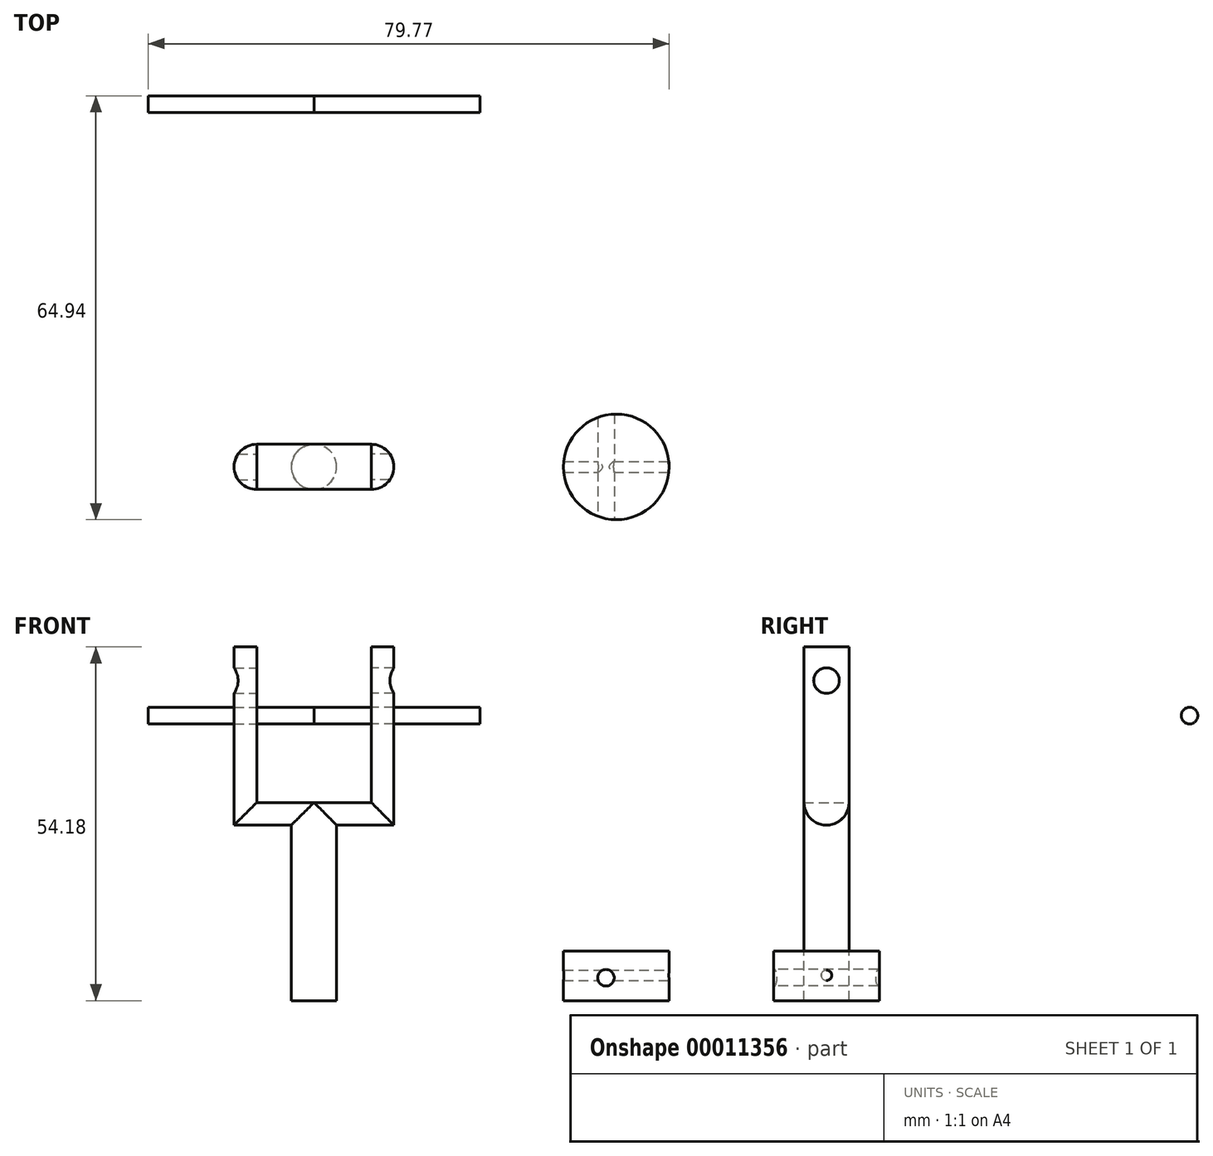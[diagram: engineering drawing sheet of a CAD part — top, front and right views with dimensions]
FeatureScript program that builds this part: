
annotation { "Feature Type Name" : "Feature", "Feature Type Description" : "" }
export const myFeature = defineFeature(function(context is Context, id is Id, definition is map)
    precondition{}
    {
        {
            var Q0;
            Q0=qCreatedBy(makeId("Front.planeOp"),FACE);
            var sketch = newSketch(context, id + "F0", { "sketchPlane" : qUnion([Q0])});
            skLineSegment(sketch, "E0", {"start": v(0, 0) * mm, "end": v(0, 30.36) * mm});
            skLineSegment(sketch, "E1", {"start": v(0, 30.36) * mm, "end": v(8.77, 30.36) * mm});
            skLineSegment(sketch, "E2", {"start": v(8.77, 30.36) * mm, "end": v(8.77, 54.18) * mm});
            skSolve(sketch);
        }
        {
            var Q0;
            Q0=qCreatedBy(makeId("Top.planeOp"),FACE);
            var sketch = newSketch(context, id + "F1", { "sketchPlane" : qUnion([Q0])});
            skArc(sketch, "E3", {"start": v(0, -3.46) * mm, "mid": v(3.46, 0) * mm, "end": v(0, 3.46) * mm});
            skLineSegment(sketch, "E4", {"start": v(0, 3.46) * mm, "end": v(0, -3.46) * mm});
            skSolve(sketch);
        }
        {
            var Q0;
            Q0=makeQuery(id+"F1.imprint","IMPRINT",FACE,{"disambiguationData":[TD([[makeQuery(id+"F1.imprint","IMPRINT",EDGE,{"derivedFrom":sQuery(id+"F1.wireOp",EDGE,"E3")}),1.0]])]});
            var Q1;
            Q1 = qBodyType(qCreatedBy(id + "F0" ,EDGE), BodyType.WIRE);
            sweep(context, id + "F2", {"profiles" : qUnion([Q0]), "path" : qUnion([Q1])});
        }
        {
            var Q0;
            Q0=qCreatedBy(makeId("Right.planeOp"),FACE);
            var sketch = newSketch(context, id + "F3", { "sketchPlane" : qUnion([Q0])});
            skCircle(sketch, "E5", {"center": v(0, 49.03) * mm, "radius": 1.97 * mm});
            skSolve(sketch);
        }
        {
            var Q0;
            Q0=makeQuery(id+"F3.imprint","IMPRINT",FACE,{"disambiguationData":[TD([[makeQuery(id+"F3.imprint","IMPRINT",EDGE,{"derivedFrom":sQuery(id+"F3.wireOp",EDGE,"E5")}),1.0]])]});
            extrude(context, id + "F4", {"entities" : qUnion([Q0]), "operationType" : NewBodyOperationType.REMOVE, "endBound" : BoundingType.THROUGH_ALL, "depth" : 25.4 * mm});
        }
        {
            var Q0;
            Q0=makeQuery(id+"F2.opSweep","SWEPT_BODY",BODY,{"disambiguationData":[OSD([sQuery(id+"F0.wireOp",EDGE,"5b2f2e84-3ed1-4c50-bd8c-a09292b5c9df"),sQuery(id+"F1.wireOp",EDGE,"E3"),sQuery(id+"F1.wireOp",EDGE,"E4")])]});
            var Q1;
            Q1=qCreatedBy(makeId("Right.planeOp"),FACE);
            mirror(context, id + "F5", {"operationType" : NewBodyOperationType.ADD, "entities" : qUnion([Q0]), "mirrorPlane" : qUnion([Q1])});
        }
        {
            var Q0;
            Q0=qCreatedBy(makeId("Right.planeOp"),FACE);
            var sketch = newSketch(context, id + "F6", { "sketchPlane" : qUnion([Q0])});
            skCircle(sketch, "E6", {"center": v(55.58, 43.67) * mm, "radius": 1.27 * mm});
            skSolve(sketch);
        }
        {
            var Q0;
            Q0 = qSketchRegion(id + "F6", true);
            extrude(context, id + "F7", {"entities" : qUnion([Q0]), "depth" : 25.4 * mm});
        }
        {
            var Q0;
            Q0=makeQuery(id+"F7.opExtrude","SWEPT_BODY",BODY,{"disambiguationData":[OSD([sQuery(id+"F6.wireOp",EDGE,"E6")])]});
            var Q1;
            Q1=qCreatedBy(makeId("Right.planeOp"),FACE);
            mirror(context, id + "F8", {"operationType" : NewBodyOperationType.ADD, "entities" : qUnion([Q0]), "mirrorPlane" : qUnion([Q1])});
        }
        {
            var Q0;
            Q0=qCreatedBy(makeId("Top.planeOp"),FACE);
            var sketch = newSketch(context, id + "F9", { "sketchPlane" : qUnion([Q0])});
            skCircle(sketch, "E7", {"center": v(46.28, 0) * mm, "radius": 8.09 * mm});
            skSolve(sketch);
        }
        {
            var Q0;
            Q0=makeQuery(id+"F9.imprint","IMPRINT",FACE,{"disambiguationData":[TD([[makeQuery(id+"F9.imprint","IMPRINT",EDGE,{"derivedFrom":sQuery(id+"F9.wireOp",EDGE,"E7")}),1.0]])]});
            extrude(context, id + "F10", {"entities" : qUnion([Q0]), "depth" : 7.62 * mm});
        }
        {
            var Q0;
            Q0=qCreatedBy(makeId("Front.planeOp"),FACE);
            var sketch = newSketch(context, id + "F11", { "sketchPlane" : qUnion([Q0])});
            skCircle(sketch, "E8", {"center": v(44.7, 3.51) * mm, "radius": 1.27 * mm});
            skSolve(sketch);
        }
        {
            var Q0;
            Q0 = qSketchRegion(id + "F11", true);
            extrude(context, id + "F12", {"entities" : qUnion([Q0]), "operationType" : NewBodyOperationType.REMOVE, "endBound" : BoundingType.UP_TO_NEXT, "oppositeDirection" : true, "depth" : 25.4 * mm});
        }
        {
            var Q0;
            Q0 = qSketchRegion(id + "F11", true);
            extrude(context, id + "F13", {"entities" : qUnion([Q0]), "operationType" : NewBodyOperationType.REMOVE, "endBound" : BoundingType.UP_TO_NEXT, "depth" : 25.4 * mm});
        }
        {
            var Q0;
            Q0=makeQuery(id+"F10.opExtrude","CAP_FACE",FACE,{"disambiguationData":[OSD([sQuery(id+"F9.wireOp",EDGE,"E7")])],"isStart":false});
            var sketch = newSketch(context, id + "F14", { "sketchPlane" : qUnion([Q0])});
            skPoint(sketch, "E9", {"position": v(46.28, 0) * mm});
            skSolve(sketch);
        }
        {
            var Q0;
            Q0=qCreatedBy(makeId("Right.planeOp"),FACE);
            var Q1;
            Q1=sQuery(id+"F14.wireOp",VERTEX,"E9");
            cPlane(context, id + "F15", {"entities" : qUnion([Q0, Q1]), "cplaneType" : CPlaneType.PLANE_POINT, "offset" : 152.4 * mm, "width" : 152.4 * mm, "height" : 152.4 * mm});
        }
        {
            var Q0;
            Q0=qCreatedBy(id+"F15.planeOp",FACE);
            var sketch = newSketch(context, id + "F16", { "sketchPlane" : qUnion([Q0])});
            skCircle(sketch, "E10", {"center": v(0, 3.87) * mm, "radius": 0.8 * mm});
            skSolve(sketch);
        }
        {
            var Q0;
            Q0 = qSketchRegion(id + "F16", true);
            extrude(context, id + "F17", {"entities" : qUnion([Q0]), "operationType" : NewBodyOperationType.REMOVE, "oppositeDirection" : true, "depth" : 25.4 * mm});
        }
        {
            var Q0;
            Q0 = qSketchRegion(id + "F16", true);
            extrude(context, id + "F18", {"entities" : qUnion([Q0]), "operationType" : NewBodyOperationType.REMOVE, "endBound" : BoundingType.UP_TO_NEXT, "depth" : 25.4 * mm});
        }
    });
